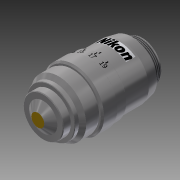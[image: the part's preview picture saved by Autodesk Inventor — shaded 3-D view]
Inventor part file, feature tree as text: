
AUTODESK INVENTOR PART (.ipt)
format: ipt  version: 2015 SP1 (Build 190203100, 203)  size: 1,977,344 bytes
history: native  units: mm
features: chamfer x7, sketch x7, extrude x3, plane x2, other x2, emboss x2, revolve x1, thread x1, shell x1, projected_geometry x1
ambient origin geometry x8: Origin, YZ Plane, XZ Plane, XY Plane, X Axis, Y Axis, Z Axis, Center Point
bodies: Solid1 (feature_tree)
feature tree (27):
  revolve  "Revolution1"  [1 undecoded]
  chamfer  "Chamfer1"  Distance=1.5mm
  chamfer  "Chamfer2"  Distance=9.7mm
  chamfer  "Chamfer3"  Distance=18.75mm
  chamfer  "Chamfer4"  Distance=18.75mm
  chamfer  "Chamfer5"  Distance=18.0mm
  extrude  "Extrusion1"  Depth=10.0mm
  extrude  "Extrusion2"  Depth=17.0mm
  extrude  "Extrusion3"  Depth=10.0mm
  thread  "Thread1"  [1 undecoded]
  chamfer  "Chamfer6"  Distance=7.9mm
  chamfer  "Chamfer7"  Distance=1.5mm
  plane  "Work Plane1"
  other  "Decal1"
  shell  "Shell1"  Thickness=13.788101mm
  plane  "Work Plane2"
  emboss  "Emboss1"
  emboss  "Emboss2"
  sketch  "Sketch1"  dims[d0=4.0mm d3=3.36mm]
  sketch  "Sketch2"  dims[d4=15.0mm]
  sketch  "Sketch3"  dims[d9=4.7mm]
  sketch  "Sketch4"  dims[d10=2.6mm]
  sketch  "Sketch6"  dims[d11=17.25mm]
  other  "Image1"
  sketch  "Sketch7"  dims[d12=2.25mm]
  sketch  "Sketch8"  dims[d13=16.7mm d14=1.5mm d15=9.7mm d16=18.75mm d17=18.75mm d18=18.0mm d19=16.0mm d20=17.0mm d21=30.6mm d22=13.5mm d23=7.9mm d24=1.5mm d26=13.788101mm d27=135.0deg d28=6.108652mm d29=90.0deg d30=0.4mm d31=2.0mm d32=45.0deg d33=0.3mm d34=2.0mm d35=45.0deg d36=1.0mm d37=2.0mm d38=45.0deg d39=0.5mm d40=2.0mm d41=45.0deg d42=0.5mm d43=2.0mm d44=45.0deg d45=23.8mm d46=1.0mm d47=0.0mm d48=24.97mm d49=3.0mm d50=0.0mm d51=23.8mm d52=1.0mm d53=0.0mm d54=10.0mm d55=0.0mm d56=0.4mm d57=2.0mm d58=45.0deg d59=0.4mm d60=2.0mm d61=45.0deg d62=20.0mm d69=2.0mm d70=20.0mm d71=40.0mm d73=7.15mm d74=10.0mm d76=10.0mm d79=40.0mm d81=10.0mm d82=0.25mm d83=0.0mm d84=0.25mm d85=0.0mm]
  projected_geometry  "Projected Loop1"
note: 2 required parameter values undecoded (feature->parameter linkage not recoverable at this tier; creation-order binding heuristic only, values carry confidence <= 0.55)